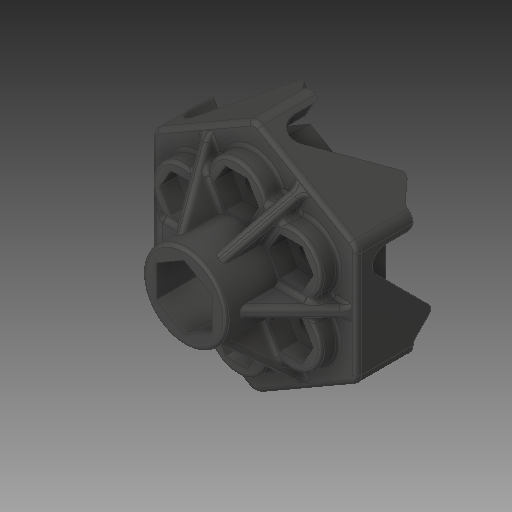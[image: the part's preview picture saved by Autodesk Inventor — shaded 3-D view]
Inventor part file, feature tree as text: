
AUTODESK INVENTOR PART (.ipt)
format: ipt  version: 2018 (Build 220112000, 112)  size: 1,374,720 bytes
history: native  units: in
note: dims shown in document units (in); Inventor stores cm internally (conversion verified against a paired STEP export)
features: fillet x1
ambient origin geometry x8: Origin, YZ Plane, XZ Plane, XY Plane, X Axis, Y Axis, Z Axis, Center Point
bodies: Solid1 (feature_tree)
feature tree (1):
  fillet  "Fillet21"  [1 undecoded]
note: 1 required parameter value undecoded (feature->parameter linkage not recoverable at this tier; creation-order binding heuristic only, values carry confidence <= 0.55)
